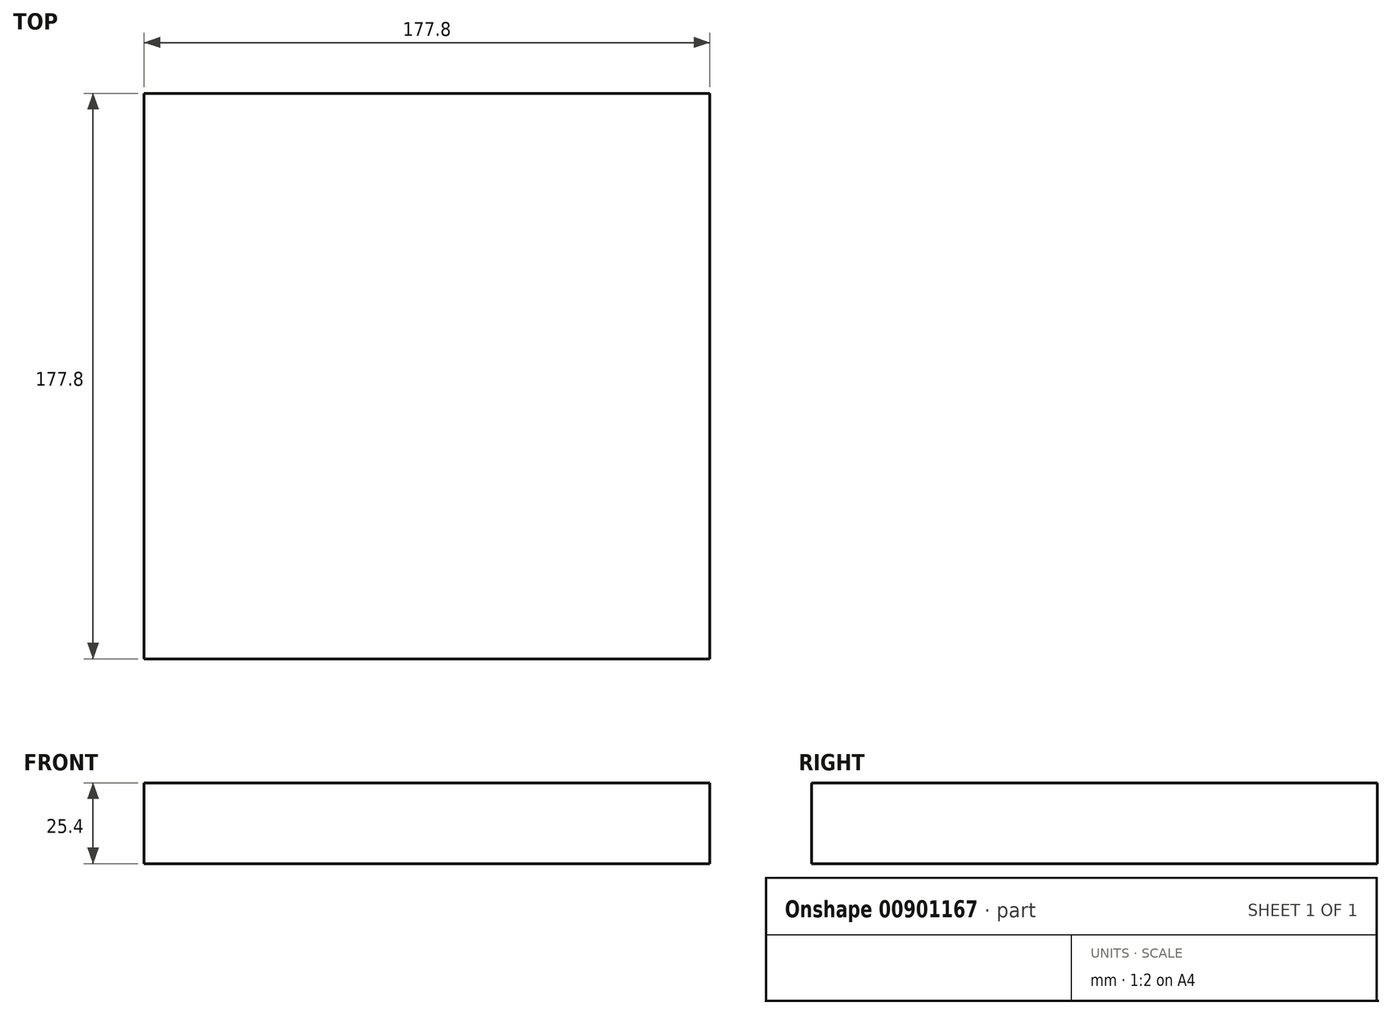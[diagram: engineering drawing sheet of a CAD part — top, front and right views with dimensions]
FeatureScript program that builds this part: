
annotation { "Feature Type Name" : "Feature", "Feature Type Description" : "" }
export const myFeature = defineFeature(function(context is Context, id is Id, definition is map)
    precondition{}
    {
        {
            var Q0;
            Q0=qCreatedBy(makeId("Top.planeOp"),FACE);
            var sketch = newSketch(context, id + "F0", { "sketchPlane" : qUnion([Q0])});
            skLineSegment(sketch, "E0.bottom", {"start": v(44.04, -22.15) * mm, "end": v(66.53, -22.15) * mm});
            skLineSegment(sketch, "E0.top", {"start": v(44.04, -66.6) * mm, "end": v(66.53, -66.6) * mm});
            skLineSegment(sketch, "E0.left", {"start": v(44.04, -22.15) * mm, "end": v(44.04, -66.6) * mm});
            skLineSegment(sketch, "E0.right", {"start": v(66.53, -22.15) * mm, "end": v(66.53, -66.6) * mm});
            skPoint(sketch, "E1.oppositeSnap0", {"position": v(44.04, -44.37) * mm});
            skLineSegment(sketch, "E1.bottom", {"start": v(-67.05, -22.15) * mm, "end": v(-44.73, -22.15) * mm});
            skLineSegment(sketch, "E1.top", {"start": v(-67.05, -44.37) * mm, "end": v(-44.73, -44.37) * mm});
            skLineSegment(sketch, "E1.left", {"start": v(-67.05, -22.15) * mm, "end": v(-67.05, -44.37) * mm});
            skLineSegment(sketch, "E1.right", {"start": v(-44.73, -22.15) * mm, "end": v(-44.73, -44.37) * mm});
            skLineSegment(sketch, "E2", {"start": v(-67.14, 67.12) * mm, "end": v(-22.43, 67.12) * mm});
            skLineSegment(sketch, "E3", {"start": v(-22.43, 67.12) * mm, "end": v(-22.43, 22.65) * mm});
            skLineSegment(sketch, "E4", {"start": v(-22.43, 22.65) * mm, "end": v(0, 22.65) * mm});
            skLineSegment(sketch, "E5", {"start": v(0, 22.65) * mm, "end": v(0, 67.12) * mm});
            skLineSegment(sketch, "E6", {"start": v(0, 67.12) * mm, "end": v(44.16, 67.12) * mm});
            skLineSegment(sketch, "E7", {"start": v(44.16, 67.12) * mm, "end": v(44.16, 44.86) * mm});
            skLineSegment(sketch, "E8", {"start": v(44.16, 44.86) * mm, "end": v(66.55, 44.86) * mm});
            skLineSegment(sketch, "E9", {"start": v(66.55, 44.86) * mm, "end": v(66.55, 22.65) * mm});
            skLineSegment(sketch, "E10", {"start": v(66.55, 22.65) * mm, "end": v(22.5, 22.65) * mm});
            skLineSegment(sketch, "E11", {"start": v(22.5, 22.65) * mm, "end": v(22.5, 0) * mm});
            skLineSegment(sketch, "E12", {"start": v(22.5, 0) * mm, "end": v(0, 0) * mm});
            skLineSegment(sketch, "E13", {"start": v(0, 0) * mm, "end": v(0, -22.3) * mm});
            skLineSegment(sketch, "E14", {"start": v(0, -22.3) * mm, "end": v(22.44, -22.3) * mm});
            skLineSegment(sketch, "E15", {"start": v(22.44, -22.3) * mm, "end": v(22.44, -44.1) * mm});
            skLineSegment(sketch, "E16", {"start": v(22.44, -44.1) * mm, "end": v(0, -44.1) * mm});
            skLineSegment(sketch, "E17", {"start": v(0, -44.1) * mm, "end": v(0, -66.6) * mm});
            skLineSegment(sketch, "E18", {"start": v(0, -66.6) * mm, "end": v(-22.43, -66.6) * mm});
            skLineSegment(sketch, "E19", {"start": v(-22.43, -66.6) * mm, "end": v(-22.43, -22.3) * mm});
            skLineSegment(sketch, "E20", {"start": v(-22.43, -22.3) * mm, "end": v(-44.73, -22.15) * mm});
            skLineSegment(sketch, "E21", {"start": v(-44.73, -22.15) * mm, "end": v(-44.73, 0) * mm});
            skLineSegment(sketch, "E22", {"start": v(-44.73, 0) * mm, "end": v(-67.05, 0) * mm});
            skLineSegment(sketch, "E23", {"start": v(-67.05, 0) * mm, "end": v(-67.05, 22.65) * mm});
            skLineSegment(sketch, "E24", {"start": v(-67.05, 22.65) * mm, "end": v(-44.73, 22.65) * mm});
            skLineSegment(sketch, "E25", {"start": v(-44.73, 22.65) * mm, "end": v(-44.73, 44.55) * mm});
            skLineSegment(sketch, "E26", {"start": v(-44.73, 44.55) * mm, "end": v(-67.05, 44.55) * mm});
            skLineSegment(sketch, "E27", {"start": v(-67.05, 44.55) * mm, "end": v(-67.14, 67.12) * mm});
            skLineSegment(sketch, "E28.bottom", {"start": v(-88.9, 88.9) * mm, "end": v(88.9, 88.9) * mm});
            skLineSegment(sketch, "E28.top", {"start": v(-88.9, -88.9) * mm, "end": v(88.9, -88.9) * mm});
            skLineSegment(sketch, "E28.left", {"start": v(-88.9, 88.9) * mm, "end": v(-88.9, -88.9) * mm});
            skLineSegment(sketch, "E28.right", {"start": v(88.9, 88.9) * mm, "end": v(88.9, -88.9) * mm});
            skSolve(sketch);
        }
        {
            var Q0;
            Q0=makeQuery(id+"F0.imprint","IMPRINT",FACE,{"disambiguationData":[TD([[makeQuery(id+"F0.imprint","IMPRINT",EDGE,{"derivedFrom":sQuery(id+"F0.wireOp",EDGE,"E0.bottom")}),1.0]])]});
            var sketch = newSketch(context, id + "F1", { "sketchPlane" : qUnion([Q0])});
            skLineSegment(sketch, "E29.0", {"start": v(-88.9, 88.9) * mm, "end": v(88.9, 88.9) * mm});
            skLineSegment(sketch, "E30.0", {"start": v(88.9, 88.9) * mm, "end": v(88.9, -88.9) * mm});
            skLineSegment(sketch, "E31.0", {"start": v(-88.9, -88.9) * mm, "end": v(88.9, -88.9) * mm});
            skLineSegment(sketch, "E32.0", {"start": v(-88.9, 88.9) * mm, "end": v(-88.9, -88.9) * mm});
            skSolve(sketch);
        }
        {
            var Q0;
            Q0 = qSketchRegion(id + "F1", true);
            extrude(context, id + "F2", {"entities" : qUnion([Q0]), "depth" : 25.4 * mm, "offsetDistance" : 25.4 * mm});
        }
        {
            var Q0;
            Q0=makeQuery(id+"F0.imprint","IMPRINT",FACE,{"disambiguationData":[TD([[makeQuery(id+"F0.imprint","IMPRINT",EDGE,{"derivedFrom":sQuery(id+"F0.wireOp",EDGE,"E2")}),-1.0]])]});
            var Q1;
            Q1=makeQuery(id+"F0.imprint","IMPRINT",FACE,{"disambiguationData":[TD([[makeQuery(id+"F0.imprint","IMPRINT",EDGE,{"derivedFrom":sQuery(id+"F0.wireOp",EDGE,"E0.bottom")}),-1.0]])]});
            var Q2;
            Q2=makeQuery(id+"F0.imprint","IMPRINT",FACE,{"disambiguationData":[TD([[makeQuery(id+"F0.imprint","IMPRINT",EDGE,{"derivedFrom":sQuery(id+"F0.wireOp",EDGE,"E1.bottom")}),-1.0]])]});
            extrude(context, id + "F3", {"entities" : qUnion([Q0, Q1, Q2]), "operationType" : NewBodyOperationType.REMOVE, "oppositeDirection" : true, "depth" : 25.4 * mm, "offsetDistance" : 25.4 * mm});
        }
    });
